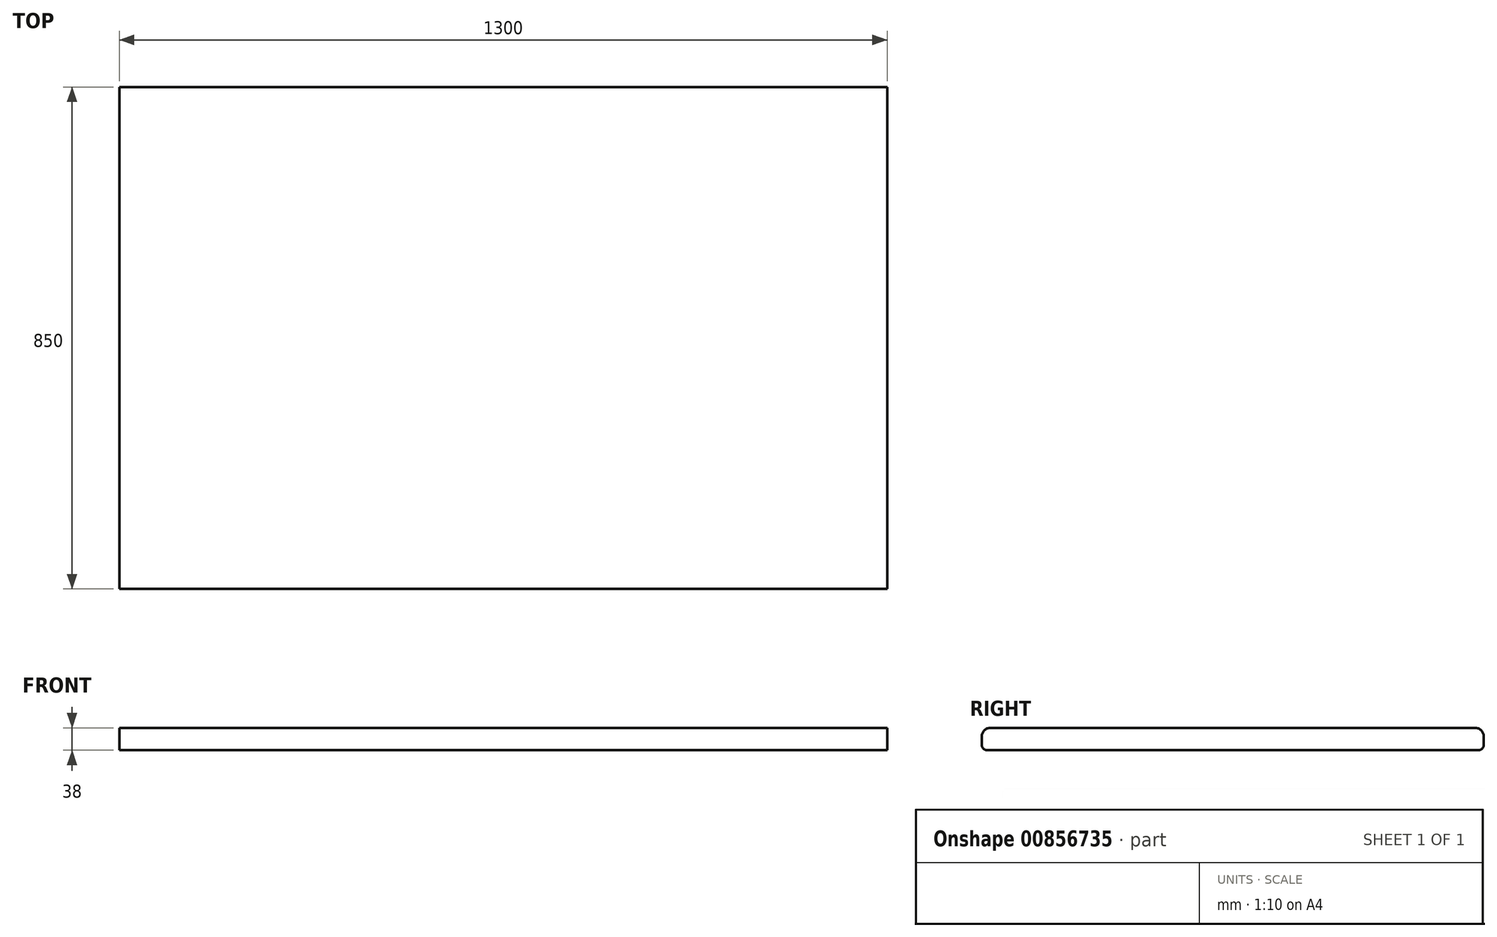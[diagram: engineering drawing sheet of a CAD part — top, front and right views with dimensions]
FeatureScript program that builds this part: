
annotation { "Feature Type Name" : "Feature", "Feature Type Description" : "" }
export const myFeature = defineFeature(function(context is Context, id is Id, definition is map)
    precondition{}
    {
        {
            var Q0;
            Q0=qCreatedBy(makeId("Top.planeOp"),FACE);
            var sketch = newSketch(context, id + "F0", { "sketchPlane" : qUnion([Q0])});
            skLineSegment(sketch, "E0.bottom", {"start": v(-701.18, -444.24) * mm, "end": v(598.82, -444.24) * mm});
            skLineSegment(sketch, "E0.top", {"start": v(-701.18, 405.76) * mm, "end": v(598.82, 405.76) * mm});
            skLineSegment(sketch, "E0.left", {"start": v(-701.18, -444.24) * mm, "end": v(-701.18, 405.76) * mm});
            skLineSegment(sketch, "E0.right", {"start": v(598.82, -444.24) * mm, "end": v(598.82, 405.76) * mm});
            skSolve(sketch);
        }
        {
            var Q0;
            Q0 = qSketchRegion(id + "F0", true);
            extrude(context, id + "F1", {"entities" : qUnion([Q0]), "depth" : 38 * mm, "offsetDistance" : 25 * mm});
        }
        {
            var Q0;
            Q0=makeQuery(id+"F1.opExtrude","CAP_EDGE",EDGE,{"disambiguationData":[OSD([sQuery(id+"F0.wireOp",EDGE,"E0.bottom")])],"isStart":false});
            fillet(context, id + "F2", {"entities" : qUnion([Q0]), "radius" : 15 * mm, "tangentPropagation" : true, "allowEdgeOverflow" : false});
        }
        {
            var Q0;
            Q0=makeQuery(id+"F1.opExtrude","CAP_EDGE",EDGE,{"disambiguationData":[OSD([sQuery(id+"F0.wireOp",EDGE,"E0.top")])],"isStart":false});
            fillet(context, id + "F3", {"entities" : qUnion([Q0]), "radius" : 15 * mm, "tangentPropagation" : true, "allowEdgeOverflow" : false});
        }
        {
            var Q0;
            Q0=makeQuery(id+"F1.opExtrude","CAP_EDGE",EDGE,{"disambiguationData":[OSD([sQuery(id+"F0.wireOp",EDGE,"E0.bottom")])],"isStart":true});
            fillet(context, id + "F4", {"entities" : qUnion([Q0]), "radius" : 10 * mm, "tangentPropagation" : true, "allowEdgeOverflow" : false});
        }
        {
            var Q0;
            Q0=makeQuery(id+"F1.opExtrude","CAP_EDGE",EDGE,{"disambiguationData":[OSD([sQuery(id+"F0.wireOp",EDGE,"E0.top")])],"isStart":true});
            fillet(context, id + "F5", {"entities" : qUnion([Q0]), "radius" : 10 * mm, "tangentPropagation" : true, "allowEdgeOverflow" : false});
        }
    });
